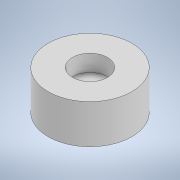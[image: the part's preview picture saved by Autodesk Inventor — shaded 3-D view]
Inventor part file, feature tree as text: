
AUTODESK INVENTOR PART (.ipt)
format: ipt  version: 2021 (Build 250183000, 183)  size: 227,328 bytes
history: native  units: mm
features: extrude x2, sketch x1
ambient origin geometry x8: Origin, YZ Plane, XZ Plane, XY Plane, X Axis, Y Axis, Z Axis, Center Point
bodies: Solid1 (feature_tree)
feature tree (3):
  sketch  "Sketch1"  dims[d0=15.0mm d1=6.25mm d2=7.0mm d3=0.0mm d4=4.0mm d5=0.0mm]
  extrude  "MainBody"  Depth=4.0mm
  extrude  "MagnetCutout"  Depth=7.0mm TaperAngle=0.0deg
